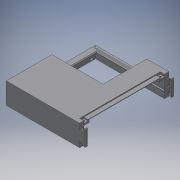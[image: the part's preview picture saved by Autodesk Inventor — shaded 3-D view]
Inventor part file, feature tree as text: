
AUTODESK INVENTOR PART (.ipt)
format: ipt  version: 2016 SP2 (Build 200236200, 236)  size: 895,488 bytes
history: native  units: mm
features: sketch x24, other x5, thread x2, revolve x2, extrude x1
ambient origin geometry x8: Origin, YZ Plane, XZ Plane, XY Plane, X Axis, Y Axis, Z Axis, Center Point
bodies: Volumenkörper2 (feature_tree), Volumenkörper3 (feature_tree), Volumenkörper1 (feature_tree)
feature tree (34):
  other  "Case_side_back.ipt"
  thread  "Gewinde1"  [1 undecoded]
  thread  "Gewinde2"  [1 undecoded]
  revolve  "Umdrehung1"
  other  "Spirale1"
  revolve  "Umdrehung2"
  other  "Spirale2"
  extrude  "Extrusion1"  Depth=0.240125mm TaperAngle=60.0deg
  other  "Volumenkörper1::Case_side_back.ipt"
  other  "Bezeichnung1"
  sketch  "Skizze1"  dims[d3=10.0mm d4=0.0mm d5=60.0deg d6=0.240125mm d7=0.240125mm]
  sketch  "Skizze2"  dims[d10=1.5mm]
  sketch  "Skizze3"  dims[d12=60.0deg]
  sketch  "Skizze4"  dims[d14=0.0mm]
  sketch  "Skizze7"  dims[d15=1.5015mm d16=7.0mm d17=10.0mm d18=0.0mm d19=0.0mm d20=0.0mm d21=0.0mm d22=0.0mm]
  sketch  "Skizze8"  dims[d23=60.0deg d24=0.240125mm d25=0.240125mm]
  sketch  "Skizze9"  dims[d28=1.5mm]
  sketch  "Skizze10"  dims[d30=60.0deg]
  sketch  "Skizze11"  dims[d32=0.0mm]
  sketch  "Skizze12"  dims[d33=1.5015mm d34=7.0mm d35=10.0mm d36=0.0mm d37=0.0mm d38=0.0mm d39=0.0mm d40=0.0mm]
  sketch  "Skizze13"  dims[d41=4.0mm]
  sketch  "Skizze14"  dims[d42=1.0mm]
  sketch  "Skizze15"  dims[d43=1.0mm]
  sketch  "Skizze16"  dims[d44=94.5mm d45=0.0mm]
  sketch  "Skizze17"
  sketch  "Skizze18"
  sketch  "Skizze19"
  sketch  "Skizze20"
  sketch  "Skizze21"
  sketch  "Skizze22"
  sketch  "Skizze23"
  sketch  "Skizze24"
  sketch  "Skizze25"
  sketch  "Skizze26"
note: 2 required parameter values undecoded (feature->parameter linkage not recoverable at this tier; creation-order binding heuristic only, values carry confidence <= 0.55)
